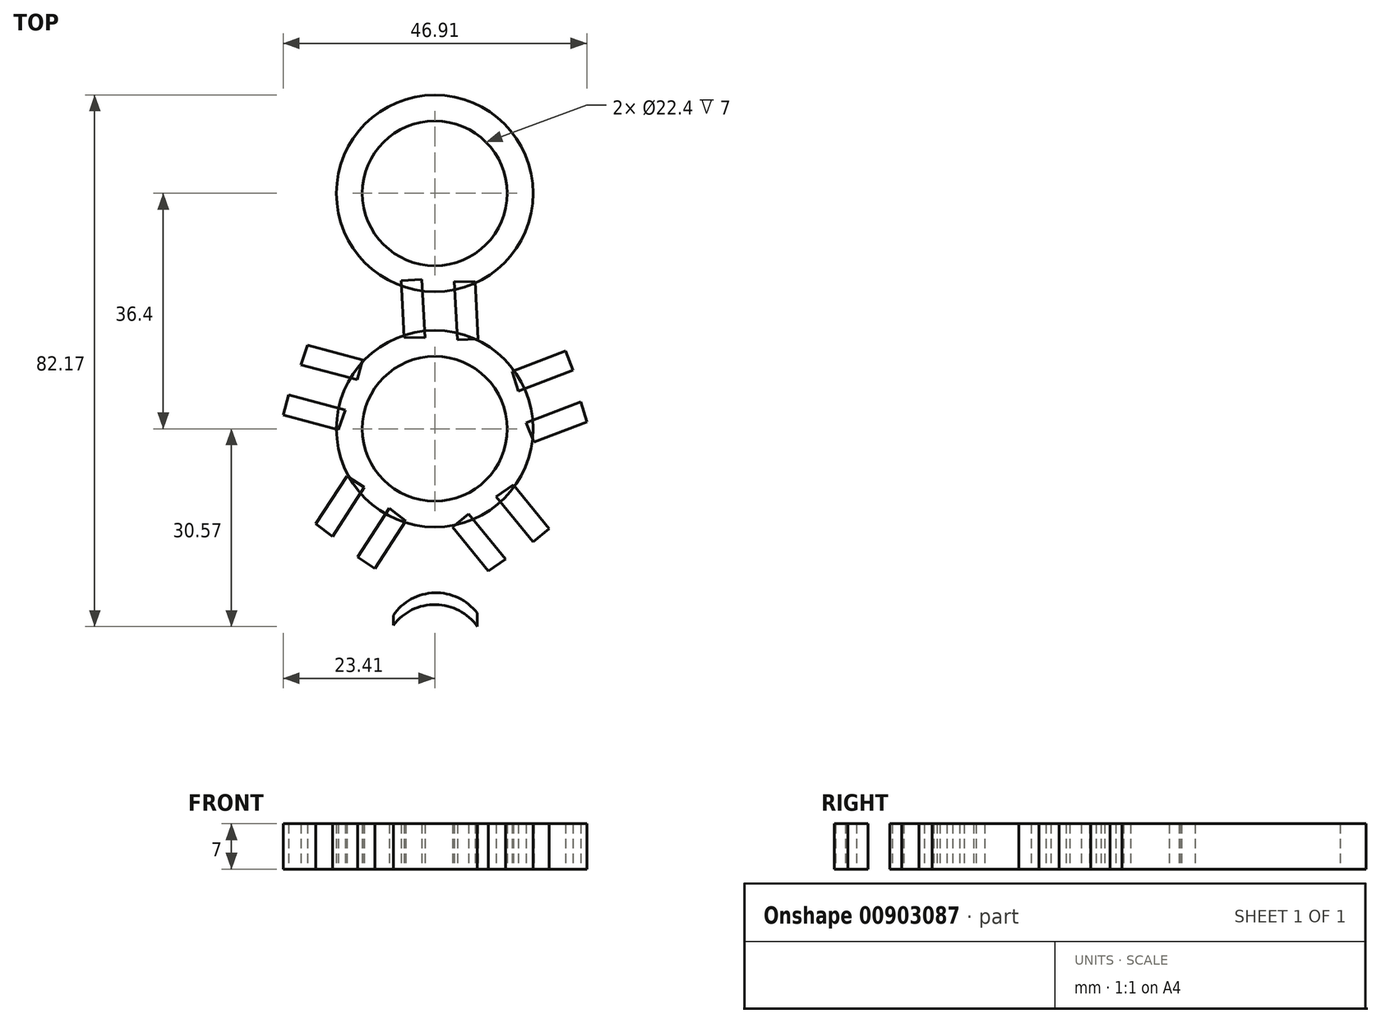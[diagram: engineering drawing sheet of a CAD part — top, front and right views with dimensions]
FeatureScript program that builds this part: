
annotation { "Feature Type Name" : "Feature", "Feature Type Description" : "" }
export const myFeature = defineFeature(function(context is Context, id is Id, definition is map)
    precondition{}
    {
        {
            var Q0;
            Q0=qCreatedBy(makeId("Top.planeOp"),FACE);
            var sketch = newSketch(context, id + "F0", { "sketchPlane" : qUnion([Q0])});
            skCircle(sketch, "E0", {"center": v(0, 0) * mm, "radius": 11.2 * mm});
            skCircle(sketch, "E1", {"center": v(0, 0) * mm, "radius": 15.2 * mm});
            skCircle(sketch, "E2", {"center": v(0, 36.4) * mm, "radius": 11.2 * mm});
            skCircle(sketch, "E3", {"center": v(0, 36.4) * mm, "radius": 15.2 * mm});
            skSolve(sketch);
        }
        {
            var Q0;
            Q0 = qSketchRegion(id + "F0", true);
            extrude(context, id + "F1", {"entities" : qUnion([Q0]), "depth" : 7 * mm, "offsetDistance" : 25 * mm});
        }
        {
            var Q0;
            Q0=qCreatedBy(makeId("Top.planeOp"),FACE);
            var sketch = newSketch(context, id + "F2", { "sketchPlane" : qUnion([Q0])});
            skArc(sketch, "E4", {"start": v(6.54, -28.48) * mm, "mid": v(-0.03, -25.36) * mm, "end": v(-6.4, -28.84) * mm});
            skArc(sketch, "E5", {"start": v(6.56, -30.57) * mm, "mid": v(0.14, -27.17) * mm, "end": v(-6.39, -30.37) * mm});
            skLineSegment(sketch, "E6", {"start": v(-6.4, -28.84) * mm, "end": v(-6.39, -30.37) * mm});
            skLineSegment(sketch, "E7", {"start": v(6.54, -28.48) * mm, "end": v(6.56, -30.57) * mm});
            skSolve(sketch);
        }
        {
            var Q0;
            Q0=makeQuery(id+"F2.imprint","IMPRINT",FACE,{"disambiguationData":[TD([[makeQuery(id+"F2.imprint","IMPRINT",EDGE,{"derivedFrom":sQuery(id+"F2.wireOp",EDGE,"E4")}),1.0]])]});
            extrude(context, id + "F3", {"entities" : qUnion([Q0]), "depth" : 7 * mm, "offsetDistance" : 25 * mm});
        }
        {
            var Q0;
            Q0=qCreatedBy(makeId("Top.planeOp"),FACE);
            var sketch = newSketch(context, id + "F4", { "sketchPlane" : qUnion([Q0])});
            skLineSegment(sketch, "E8", {"start": v(-19.65, 12.94) * mm, "end": v(-11.15, 10.67) * mm});
            skLineSegment(sketch, "E9", {"start": v(-11.15, 10.67) * mm, "end": v(-11.98, 7.57) * mm});
            skLineSegment(sketch, "E10", {"start": v(-11.98, 7.57) * mm, "end": v(-20.7, 9.9) * mm});
            skLineSegment(sketch, "E11", {"start": v(-20.7, 9.9) * mm, "end": v(-19.65, 12.94) * mm});
            skLineSegment(sketch, "E12", {"start": v(-14.9, -0.14) * mm, "end": v(-23.4, 2.12) * mm});
            skLineSegment(sketch, "E13", {"start": v(-23.4, 2.12) * mm, "end": v(-22.58, 5.23) * mm});
            skLineSegment(sketch, "E14", {"start": v(-22.58, 5.23) * mm, "end": v(-13.85, 2.9) * mm});
            skLineSegment(sketch, "E15", {"start": v(-13.85, 2.9) * mm, "end": v(-14.9, -0.14) * mm});
            skSolve(sketch);
        }
        {
            var Q0;
            Q0=makeQuery(id+"F4.imprint","IMPRINT",FACE,{"disambiguationData":[TD([[makeQuery(id+"F4.imprint","IMPRINT",EDGE,{"derivedFrom":sQuery(id+"F4.wireOp",EDGE,"E8")}),-1.0]])]});
            var Q1;
            Q1=makeQuery(id+"F4.imprint","IMPRINT",FACE,{"disambiguationData":[TD([[makeQuery(id+"F4.imprint","IMPRINT",EDGE,{"derivedFrom":sQuery(id+"F4.wireOp",EDGE,"E12")}),-1.0]])]});
            extrude(context, id + "F5", {"entities" : qUnion([Q0, Q1]), "depth" : 7 * mm, "offsetDistance" : 25 * mm});
        }
        {
            var Q0;
            Q0=makeQuery(id+"F5.opExtrude","SWEPT_BODY",BODY,{"disambiguationData":[OSD([sQuery(id+"F4.wireOp",EDGE,"E8"),sQuery(id+"F4.wireOp",EDGE,"E9"),sQuery(id+"F4.wireOp",EDGE,"E10"),sQuery(id+"F4.wireOp",EDGE,"E11")])]});
            var Q1;
            Q1=makeQuery(id+"F5.opExtrude","SWEPT_BODY",BODY,{"disambiguationData":[OSD([sQuery(id+"F4.wireOp",EDGE,"E12"),sQuery(id+"F4.wireOp",EDGE,"E13"),sQuery(id+"F4.wireOp",EDGE,"E14"),sQuery(id+"F4.wireOp",EDGE,"E15")])]});
            var Q2;
            Q2=makeQuery(id+"F1.opExtrude","CAP_EDGE",EDGE,{"disambiguationData":[OSD([sQuery(id+"F0.wireOp",EDGE,"E0")])],"isStart":false});
            circularPattern(context, id + "F6", {"entities" : qUnion([Q0, Q1]), "axis" : qUnion([Q2]), "angle" : 360 * degree, "instanceCount" : 5, "equalSpace" : true});
        }
        {
            var Q0;
            Q0=qCreatedBy(makeId("Right.planeOp"),FACE);
            cPlane(context, id + "F7", {"entities" : qUnion([Q0]), "cplaneType" : CPlaneType.OFFSET, "offset" : 57.5 * mm, "width" : 150 * mm, "height" : 150 * mm});
        }
        {
            var Q0;
            Q0=qCreatedBy(id+"F7.planeOp",FACE);
            var sketch = newSketch(context, id + "F8", { "sketchPlane" : qUnion([Q0])});
            skText(sketch, "E16", { "text": "DAA", "fontName": "AllertaStencil-Regular.ttf"});
            const initialGuessF8  = {"E16": [0.007, 0.00115, 1, 0, 0.00528]};
            skSetInitialGuess(sketch, initialGuessF8);
            skSolve(sketch);
        }
        {
            var Q0;
            Q0 = qSketchRegion(id + "F8", true);
            extrude(context, id + "F9", {"entities" : qUnion([Q0]), "operationType" : NewBodyOperationType.REMOVE, "oppositeDirection" : true, "depth" : 25 * mm, "offsetDistance" : 25 * mm});
        }
    });
